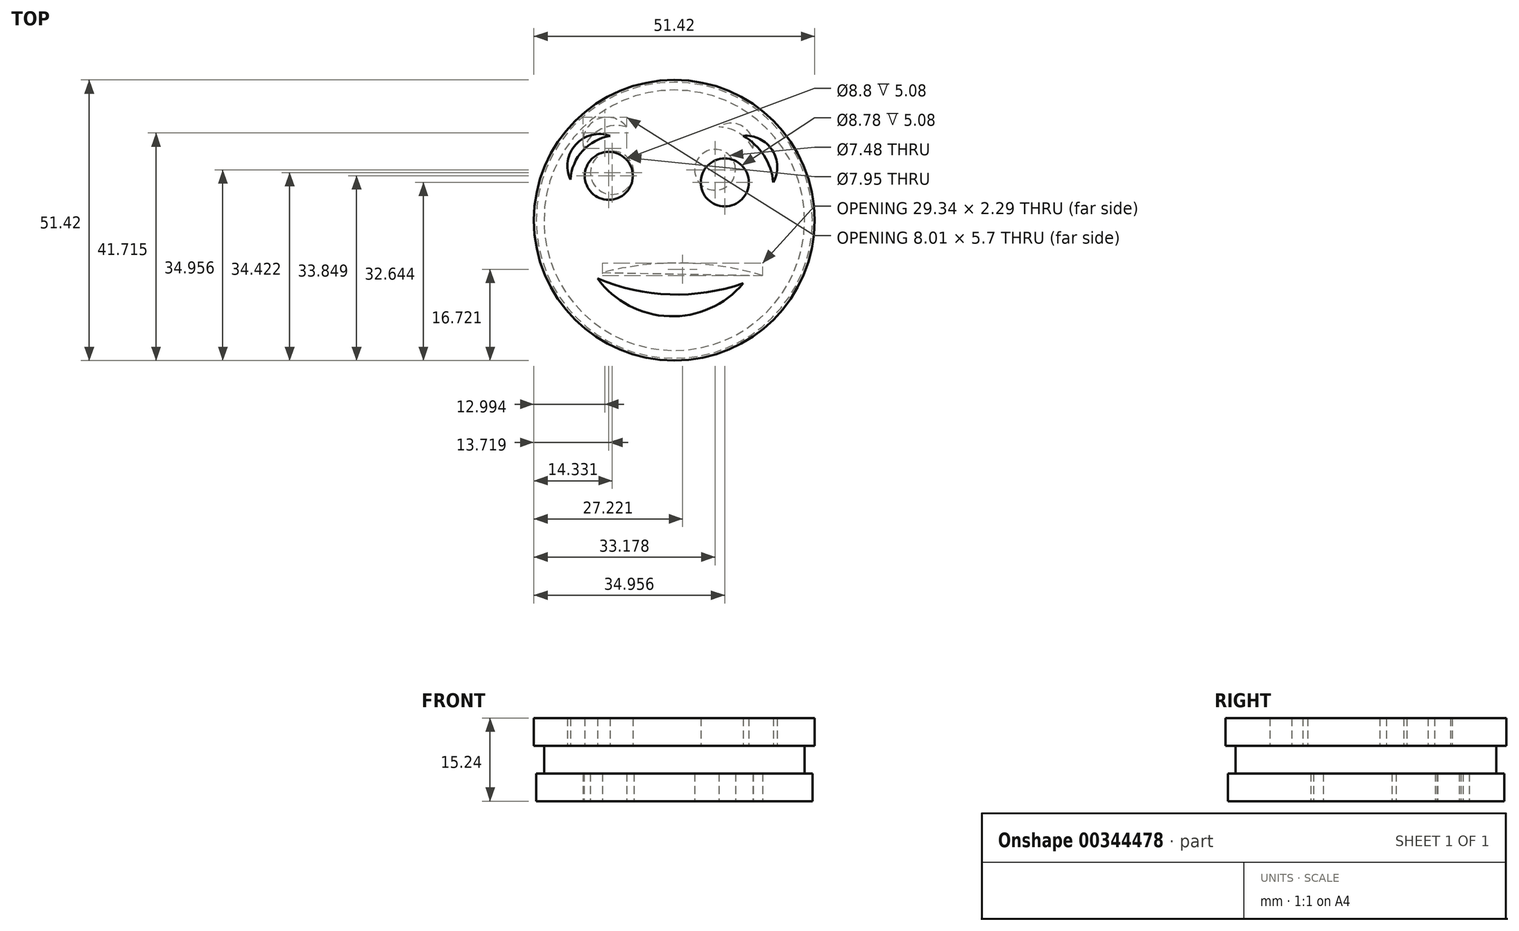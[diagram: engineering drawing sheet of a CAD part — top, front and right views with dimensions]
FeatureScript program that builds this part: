
annotation { "Feature Type Name" : "Feature", "Feature Type Description" : "" }
export const myFeature = defineFeature(function(context is Context, id is Id, definition is map)
    precondition{}
    {
        {
            var Q0;
            Q0=qCreatedBy(makeId("Top.planeOp"),FACE);
            var sketch = newSketch(context, id + "F0", { "sketchPlane" : qUnion([Q0])});
            skCircle(sketch, "E0", {"center": v(0, 0) * mm, "radius": 25.3 * mm});
            skCircle(sketch, "E1", {"center": v(7.47, 9.25) * mm, "radius": 3.74 * mm});
            skCircle(sketch, "E2", {"center": v(-11.38, 8.71) * mm, "radius": 3.98 * mm});
            skArc(sketch, "E3", {"start": v(16.18, -10.13) * mm, "mid": v(1.55, -7.84) * mm, "end": v(-13.16, -9.6) * mm});
            skLineSegment(sketch, "E4", {"start": v(-13.16, -9.6) * mm, "end": v(16.18, -10.13) * mm});
            skArc(sketch, "E5", {"start": v(-8.71, 17.07) * mm, "mid": v(-14.27, 18.41) * mm, "end": v(-16.54, 13.16) * mm});
            skArc(sketch, "E6", {"start": v(-8.71, 17.07) * mm, "mid": v(-13.41, 16.7) * mm, "end": v(-16.54, 13.16) * mm});
            skArc(sketch, "E7", {"start": v(14.4, 13.16) * mm, "mid": v(12.59, 17.17) * mm, "end": v(8.18, 17.07) * mm});
            skArc(sketch, "E8", {"start": v(14.4, 13.16) * mm, "mid": v(11.84, 15.99) * mm, "end": v(8.18, 17.07) * mm});
            skSolve(sketch);
        }
        {
            var Q0;
            Q0=makeQuery(id+"F0.imprint","IMPRINT",FACE,{"disambiguationData":[TD([[makeQuery(id+"F0.imprint","IMPRINT",EDGE,{"derivedFrom":sQuery(id+"F0.wireOp",EDGE,"E0")}),1.0]])]});
            extrude(context, id + "F1", {"entities" : qUnion([Q0]), "depth" : 5.08 * mm});
        }
        {
            var Q0;
            Q0=makeQuery(id+"F1.opExtrude","CAP_FACE",FACE,{"disambiguationData":[OSD([sQuery(id+"F0.wireOp",EDGE,"E0"),sQuery(id+"F0.wireOp",EDGE,"E1"),sQuery(id+"F0.wireOp",EDGE,"E2"),sQuery(id+"F0.wireOp",EDGE,"E3"),sQuery(id+"F0.wireOp",EDGE,"E4"),sQuery(id+"F0.wireOp",EDGE,"E5"),sQuery(id+"F0.wireOp",EDGE,"E6"),sQuery(id+"F0.wireOp",EDGE,"E7"),sQuery(id+"F0.wireOp",EDGE,"E8")])],"isStart":false});
            var sketch = newSketch(context, id + "F2", { "sketchPlane" : qUnion([Q0])});
            skCircle(sketch, "E9", {"center": v(0, 0) * mm, "radius": 23.86 * mm});
            skSolve(sketch);
        }
        {
            var Q0;
            Q0 = qSketchRegion(id + "F2", true);
            extrude(context, id + "F3", {"entities" : qUnion([Q0]), "depth" : 5.08 * mm});
        }
        {
            var Q0;
            Q0=makeQuery(id+"F3.opExtrude","CAP_FACE",FACE,{"disambiguationData":[OSD([sQuery(id+"F2.wireOp",EDGE,"E9")])],"isStart":false});
            var sketch = newSketch(context, id + "F4", { "sketchPlane" : qUnion([Q0])});
            skCircle(sketch, "E10", {"center": v(0, 0) * mm, "radius": 25.71 * mm});
            skCircle(sketch, "E11", {"center": v(-12, 8.14) * mm, "radius": 4.4 * mm});
            skCircle(sketch, "E12", {"center": v(9.25, 6.93) * mm, "radius": 4.4 * mm});
            skArc(sketch, "E13", {"start": v(-11.73, 15.47) * mm, "mid": v(-18.03, 13.89) * mm, "end": v(-19.02, 7.47) * mm});
            skArc(sketch, "E14", {"start": v(-11.73, 15.47) * mm, "mid": v(-16.78, 12.74) * mm, "end": v(-19.02, 7.47) * mm});
            skArc(sketch, "E15", {"start": v(18.14, 6.93) * mm, "mid": v(17.93, 12.85) * mm, "end": v(12.62, 15.47) * mm});
            skArc(sketch, "E16", {"start": v(18.14, 6.93) * mm, "mid": v(16.41, 11.87) * mm, "end": v(12.62, 15.47) * mm});
            skArc(sketch, "E17", {"start": v(-14.05, -10.67) * mm, "mid": v(-0.93, -17.6) * mm, "end": v(12.62, -11.56) * mm});
            skArc(sketch, "E18", {"start": v(-14.05, -10.67) * mm, "mid": v(-0.8, -13.6) * mm, "end": v(12.62, -11.56) * mm});
            skSolve(sketch);
        }
        {
            var Q0;
            Q0 = qSketchRegion(id + "F4", true);
            var Q1;
            Q1=makeQuery(id+"F4.imprint","IMPRINT",FACE,{"disambiguationData":[TD([[makeQuery(id+"F4.imprint","IMPRINT",EDGE,{"derivedFrom":sQuery(id+"F4.wireOp",EDGE,"E11")}),-1.0]])]});
            extrude(context, id + "F5", {"entities" : qUnion([Q0, Q1]), "operationType" : NewBodyOperationType.ADD, "depth" : 5.08 * mm});
        }
    });
